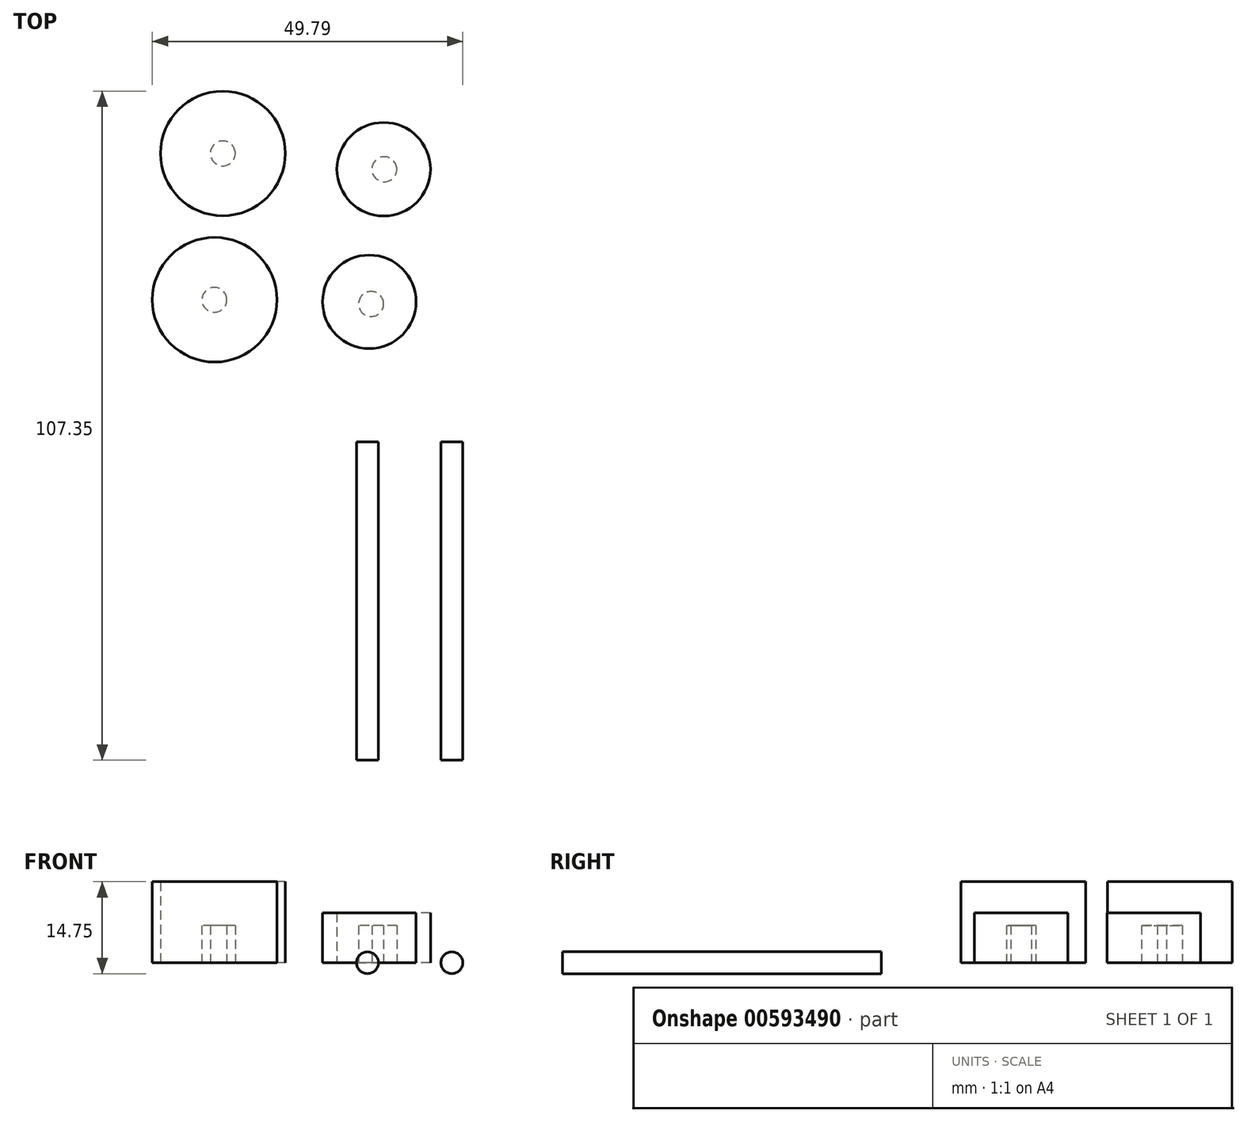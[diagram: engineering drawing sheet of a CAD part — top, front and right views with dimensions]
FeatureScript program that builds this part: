
annotation { "Feature Type Name" : "Feature", "Feature Type Description" : "" }
export const myFeature = defineFeature(function(context is Context, id is Id, definition is map)
    precondition{}
    {
        {
            var Q0;
            Q0=qCreatedBy(makeId("Front.planeOp"),FACE);
            var sketch = newSketch(context, id + "F0", { "sketchPlane" : qUnion([Q0])});
            skCircle(sketch, "E0", {"center": v(-17.28, 0) * mm, "radius": 1.75 * mm});
            skSolve(sketch);
        }
        {
            var Q0;
            Q0 = qSketchRegion(id + "F0", true);
            extrude(context, id + "F1", {"entities" : qUnion([Q0]), "depth" : 51.1 * mm, "offsetDistance" : 25.4 * mm});
        }
        {
            var Q0;
            Q0=qCreatedBy(makeId("Top.planeOp"),FACE);
            var sketch = newSketch(context, id + "F2", { "sketchPlane" : qUnion([Q0])});
            skCircle(sketch, "E1", {"center": v(-30.52, 22.44) * mm, "radius": 7.5 * mm});
            skCircle(sketch, "E2", {"center": v(-28.21, 43.71) * mm, "radius": 7.5 * mm});
            skSolve(sketch);
        }
        {
            var Q0;
            Q0 = qSketchRegion(id + "F2", true);
            extrude(context, id + "F3", {"entities" : qUnion([Q0]), "depth" : 8 * mm, "offsetDistance" : 25 * mm});
        }
        {
            var Q0;
            Q0=qCreatedBy(makeId("Top.planeOp"),FACE);
            var sketch = newSketch(context, id + "F4", { "sketchPlane" : qUnion([Q0])});
            skCircle(sketch, "E3", {"center": v(-54.01, 46.25) * mm, "radius": 10 * mm});
            skCircle(sketch, "E4", {"center": v(-55.32, 22.77) * mm, "radius": 10 * mm});
            skSolve(sketch);
        }
        {
            var Q0;
            Q0 = qSketchRegion(id + "F4", true);
            extrude(context, id + "F5", {"entities" : qUnion([Q0]), "depth" : 13 * mm, "offsetDistance" : 25 * mm});
        }
        {
            var Q0;
            Q0=qCreatedBy(makeId("Top.planeOp"),FACE);
            var sketch = newSketch(context, id + "F6", { "sketchPlane" : qUnion([Q0])});
            skCircle(sketch, "E5", {"center": v(-54.01, 46.25) * mm, "radius": 2 * mm});
            skCircle(sketch, "E6", {"center": v(-28.1, 43.7) * mm, "radius": 2 * mm});
            skCircle(sketch, "E7", {"center": v(-30.23, 22.1) * mm, "radius": 2 * mm});
            skCircle(sketch, "E8", {"center": v(-55.37, 22.76) * mm, "radius": 2 * mm});
            skSolve(sketch);
        }
        {
            var Q0;
            Q0=qCreatedBy(makeId("Front.planeOp"),FACE);
            var sketch = newSketch(context, id + "F7", { "sketchPlane" : qUnion([Q0])});
            skCircle(sketch, "E9", {"center": v(-30.8, 0) * mm, "radius": 1.75 * mm});
            skSolve(sketch);
        }
        {
            var Q0;
            Q0 = qSketchRegion(id + "F7", true);
            extrude(context, id + "F8", {"entities" : qUnion([Q0]), "depth" : 51.1 * mm, "offsetDistance" : 25 * mm});
        }
        {
            var Q0;
            Q0 = qSketchRegion(id + "F6", true);
            extrude(context, id + "F9", {"entities" : qUnion([Q0]), "depth" : 6 * mm, "offsetDistance" : 25 * mm});
        }
    });
